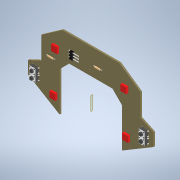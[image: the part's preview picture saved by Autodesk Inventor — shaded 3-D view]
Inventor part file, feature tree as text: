
AUTODESK INVENTOR PART (.ipt)
format: ipt  version: 2021 (Build 250183000, 183)  size: 1,277,440 bytes
history: native  units: in
note: dims shown in document units (in); Inventor stores cm internally (conversion verified against a paired STEP export)
features: other x12, plane x1
ambient origin geometry x8: Origin, YZ Plane, XZ Plane, XY Plane, X Axis, Y Axis, Z Axis, Center Point
bodies: Solid1 (feature_tree), Solid2 (feature_tree), Solid3 (feature_tree), Solid4 (feature_tree), Solid5 (feature_tree), Solid6 (feature_tree), Solid7 (feature_tree), Solid8 (feature_tree), Solid9 (feature_tree), Solid10 (feature_tree), Solid11 (feature_tree), Solid12 (feature_tree)
feature tree (13):
  plane  "Work Plane1"
  other  "Board_1:1"
  other  "7_R1:1"
  other  "7_R2:1"
  other  "B3F-10XX_S1:1"
  other  "B3F-10XX_S2:1"
  other  "B3F-10XX_S3:1"
  other  "B3F-10XX_S4:1"
  other  "90_JP2:1"
  other  "3,6-PAD_H1:1"
  other  "3,6-PAD_H2:1"
  other  "3,6-PAD_H3:1"
  other  "3,6-PAD_H4:1"
